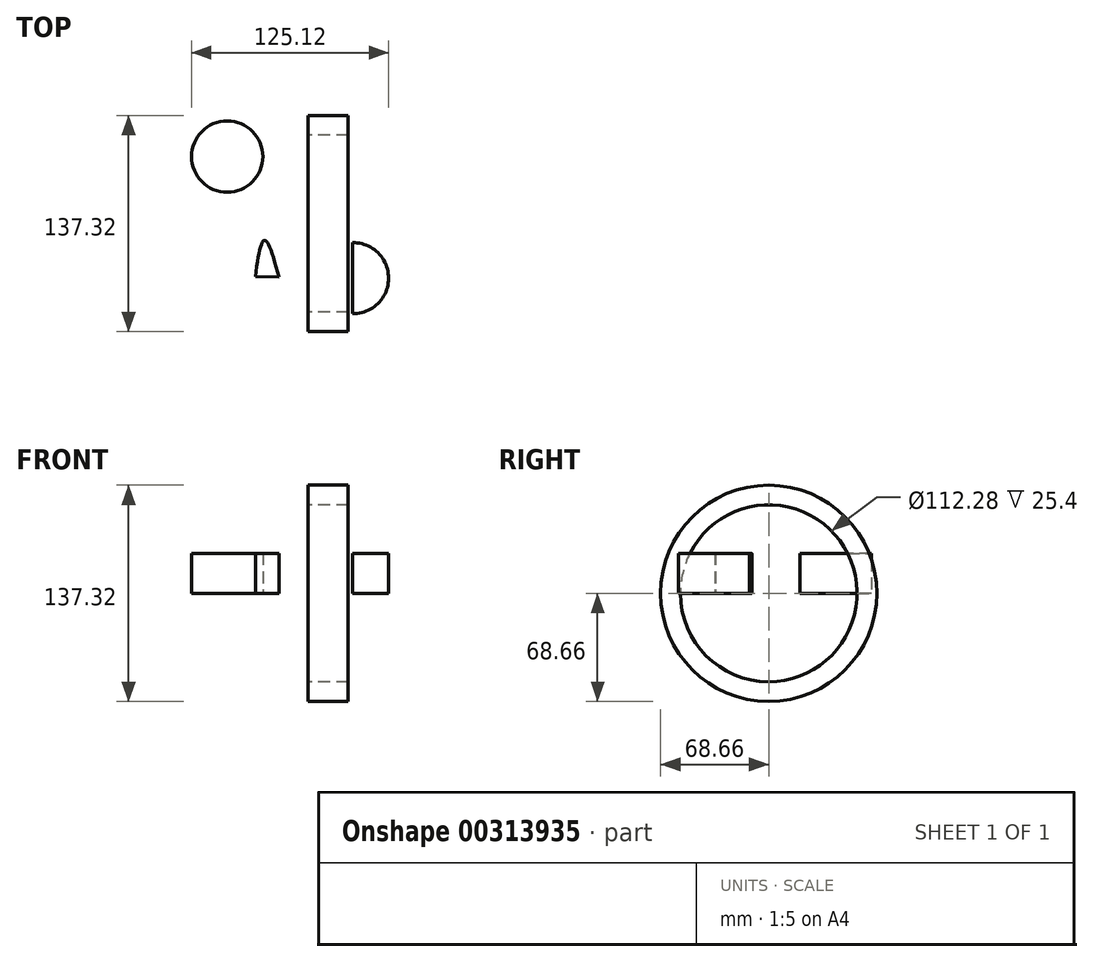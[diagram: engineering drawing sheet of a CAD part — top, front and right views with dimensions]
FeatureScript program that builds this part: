
annotation { "Feature Type Name" : "Feature", "Feature Type Description" : "" }
export const myFeature = defineFeature(function(context is Context, id is Id, definition is map)
    precondition{}
    {
        {
            var Q0;
            Q0=qCreatedBy(makeId("Top.planeOp"),FACE);
            var sketch = newSketch(context, id + "F0", { "sketchPlane" : qUnion([Q0])});
            skCircle(sketch, "E0", {"center": v(-51.4, 42.56) * mm, "radius": 22.64 * mm});
            skFitSpline(sketch, "E1", {"points": [v(0, 61.87) * mm, v(-20.7, 58.84) * mm, v(4.19, 42.56) * mm, v(-16.98, 25.35) * mm], "startDerivative": vector(-111.22, -1.69) * mm, "endDerivative": vector(-106.25, -48.96) * mm});
            skFitSpline(sketch, "E2", {"points": [v(55.36, 59.3) * mm, v(16.75, 41.87) * mm, v(56.98, 23.03) * mm], "startDerivative": vector(-117.1, -34.83) * mm, "endDerivative": vector(119.42, -37.72) * mm});
            skLineSegment(sketch, "E3", {"start": v(-70.94, -8.14) * mm, "end": v(-70.94, -56.75) * mm});
            skLineSegment(sketch, "E4", {"start": v(-70.94, -56.75) * mm, "end": v(-39.77, -56.75) * mm});
            skFitSpline(sketch, "E5", {"points": [v(-35.82, -56.52) * mm, v(-27.68, -10.7) * mm, v(-13.02, -57.68) * mm], "startDerivative": vector(13.46, 138.7) * mm, "endDerivative": vector(32.04, -139.72) * mm});
            skLineSegment(sketch, "E6", {"start": v(-33.6, -33.73) * mm, "end": v(-18.44, -34.07) * mm});
            skFitSpline(sketch, "E7", {"points": [v(-3.49, -57.22) * mm, v(1.63, -13.26) * mm, v(18.6, -56.52) * mm], "startDerivative": vector(4.63, 132.1) * mm, "endDerivative": vector(39.42, -129.63) * mm});
            skLineSegment(sketch, "E8", {"start": v(-3.49, -57.22) * mm, "end": v(-3.49, -9.3) * mm});
            skLineSegment(sketch, "E9", {"start": v(28.14, -12.1) * mm, "end": v(28.14, -57.22) * mm});
            skArc(sketch, "E10", {"start": v(28.14, -57.22) * mm, "mid": v(51.08, -34.66) * mm, "end": v(28.14, -12.1) * mm});
            skSolve(sketch);
        }
        {
            var Q0;
            Q0 = qSketchRegion(id + "F0", true);
            extrude(context, id + "F1", {"entities" : qUnion([Q0]), "depth" : 25.4 * mm});
        }
        {
            var Q0;
            Q0=qCreatedBy(makeId("Right.planeOp"),FACE);
            var sketch = newSketch(context, id + "F2", { "sketchPlane" : qUnion([Q0])});
            skCircle(sketch, "E11", {"center": v(0, 0) * mm, "radius": 68.66 * mm});
            skCircle(sketch, "E12", {"center": v(0, 0) * mm, "radius": 56.14 * mm});
            skCircle(sketch, "E13", {"center": v(0, 0) * mm, "radius": 36.38 * mm});
            skSolve(sketch);
        }
        {
            var Q0;
            Q0 = qSketchRegion(id + "F2", true);
            extrude(context, id + "F3", {"entities" : qUnion([Q0]), "depth" : 25.4 * mm});
        }
    });
